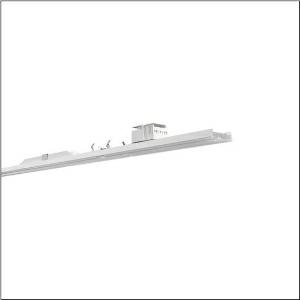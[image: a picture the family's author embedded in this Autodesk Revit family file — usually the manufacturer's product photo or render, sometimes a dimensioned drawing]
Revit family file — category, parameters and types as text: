
# Revit family: licross_r__21_recessed_mo_52tl12dne75f_abc3
name_source: partatom
category: Lighting Fixtures
units: mm (PartAtom-declared; Revit-internal decimal feet)

## family parameters
Cut with Voids When Loaded = No
Host = Face
Light Source = No
Part Type = Normal
Room Calculation Point = No
Round Connector Dimension = Use Diameter
Shared = No

## types (1)
- --- (1 x LED, 7970 lm, 61.1 W, 5000K)
    Apparent Load = 61 VA
    CIE Flux Codes = 72 92 99 100 100
    Color Rendering = 90
    Color Temperature = 5000K
    Default Elevation = 1800 mm
    Description = Licross® 21 Recessed MO, luminaire insert, of sheet steel, galvanised, coil coated, white, length: 1.500mm, width: 66mm, height: 67mm, LED rated luminous flux: 7.970lm, light colour: 950, control gear: DALI 2, control gear: ECG DALI, with plug, 5-pole, with phase selection, mains connection: 220..240V, AC, 50/60Hz, halogen-free wiring, primary optical cover: cover, of PMMA, light emission: direct distribution, protection rating (complete): IP40, insulation class (complete): insulation class I (protective earthing), certification: CE, ENEC, VDE, UKCA, protection symbol: D if used in an environment without relevant dust loads with corresponding accessories, permissible ambient temperature for indoor applications: -25..+35°C, corresponds to IFS (International Featured Standards) requirements for safety and quality in the food industry, reducing of maximum allowable ambient temperature of 5°C with ceiling mounting, packaging unit: 1 piece
    Height = 58 mm
    Lamp = 1 x LED
    Lamp Light Flux = 7970 lm
    Lamp Power = 61.1 W
    Lamp count = 1
    Length = 1500 mm
    Luminous efficacy = 130 lm/W
    Manufacturer = Siteco
    ModVariant = No
    Model = 52TL12DNE75F
    Mounting Place = Ceiling
    Mounting Type = Pendant
    Number of Poles = 1
    OnlyDefault = Yes
    Power Factor = 1
    Product Name = Licross® 21 Recessed MO
    Product group = luminaire insert
    ProductGroupID = 902
    Protection Class = Protection class I
    Protection Degree = IP 40
    RLX_Detail_Level = 1
    RlxData = <blob elided: 22485 chars, md5=203bc640>
    Socket = socket
    Standby Power = 0 W
    System Light Flux = 7970 lm
    System Power = 61 W
    Type Comments = factory setting: luminous flux: 100 % | dim-lin: 254 | 405 mA
    Type Image = l_1266722.jpg
    URL = http://relux.com
    VarID = @adj_128819
    Voltage = 0 V
    Weight = 0.00 kg
    Width = 66 mm

## geometry (parser evidence)
native form markers: Blend x4, Sweep x10
no freeform markers — native parametric forms only
